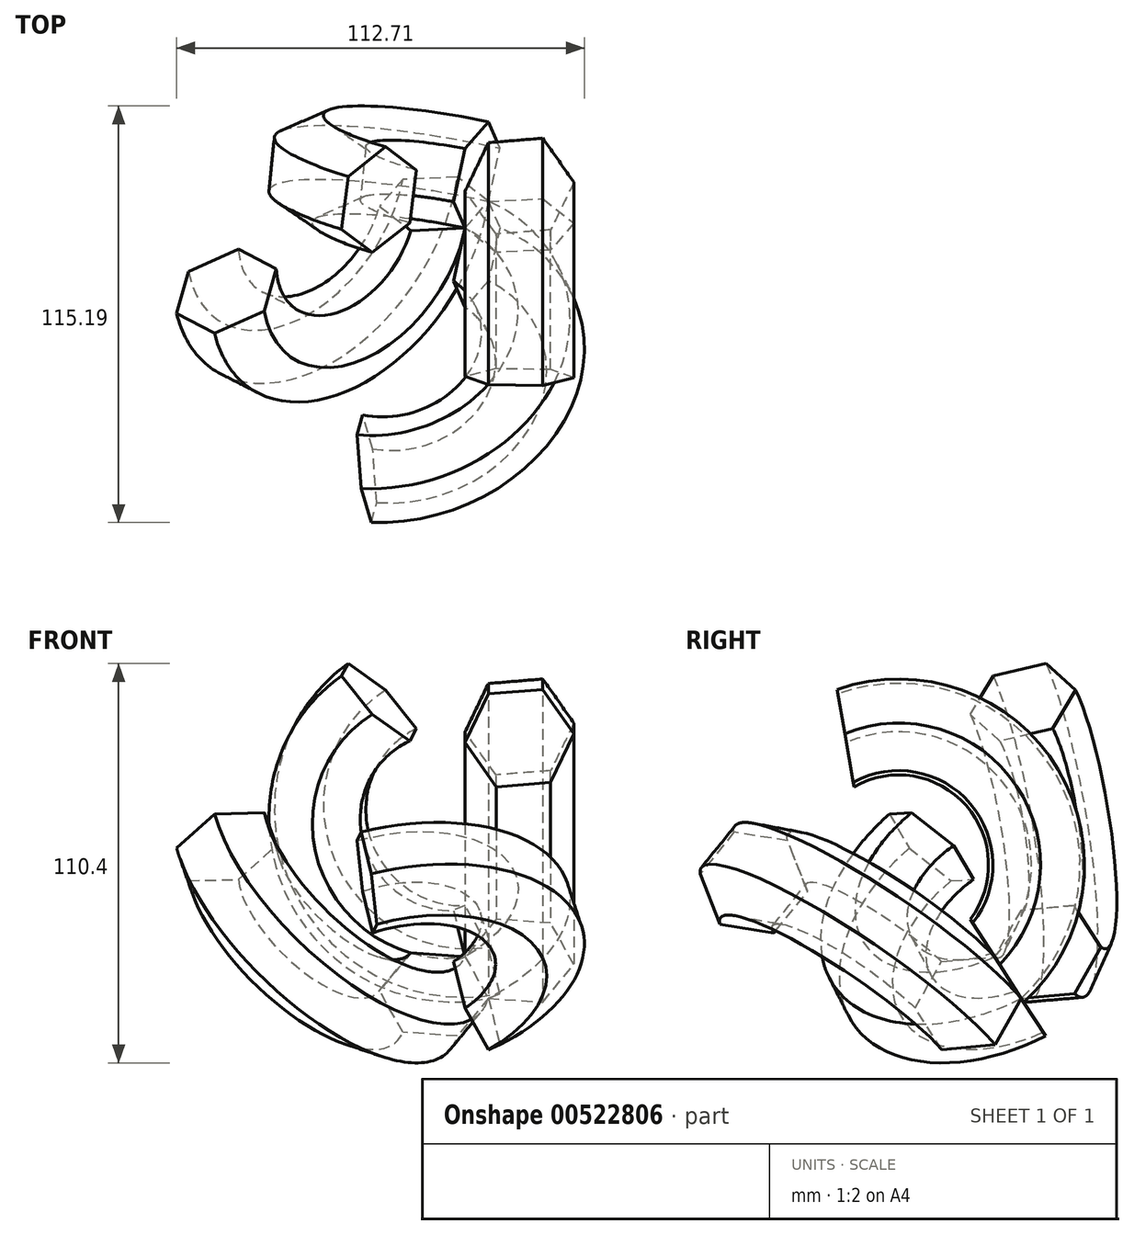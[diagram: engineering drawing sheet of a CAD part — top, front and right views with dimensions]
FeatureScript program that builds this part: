
annotation { "Feature Type Name" : "Feature", "Feature Type Description" : "" }
export const myFeature = defineFeature(function(context is Context, id is Id, definition is map)
    precondition{}
    {
        {
            var Q0;
            Q0=qCreatedBy(makeId("Top.planeOp"),FACE);
            var sketch = newSketch(context, id + "F0", { "sketchPlane" : qUnion([Q0])});
            skCircle(sketch, "E0.cCircle", {"center": v(-29.22, 20.18) * mm, "radius": 13.07 * mm, "construction": true});
            skLineSegment(sketch, "E0.0", {"start": v(-14.18, 21.44) * mm, "end": v(-20.6, 7.78) * mm});
            skLineSegment(sketch, "E0.1", {"start": v(-20.6, 7.78) * mm, "end": v(-35.65, 6.52) * mm});
            skLineSegment(sketch, "E0.2", {"start": v(-35.65, 6.52) * mm, "end": v(-44.26, 18.91) * mm});
            skLineSegment(sketch, "E0.3", {"start": v(-44.26, 18.91) * mm, "end": v(-37.84, 32.57) * mm});
            skLineSegment(sketch, "E0.4", {"start": v(-37.84, 32.57) * mm, "end": v(-22.8, 33.83) * mm});
            skLineSegment(sketch, "E0.5", {"start": v(-22.8, 33.83) * mm, "end": v(-14.18, 21.44) * mm});
            skPoint(sketch, "E0.0.midPoint", {"position": v(-17.4, 14.61) * mm});
            skSolve(sketch);
        }
        {
            var Q0;
            Q0=qCreatedBy(makeId("Right.planeOp"),FACE);
            var sketch = newSketch(context, id + "F1", { "sketchPlane" : qUnion([Q0])});
            skArc(sketch, "E1", {"start": v(-20.47, 12.8) * mm, "mid": v(-38.44, -7.8) * mm, "end": v(-21.86, -29.52) * mm});
            skSolve(sketch);
        }
        {
            var Q0;
            Q0=makeQuery(id+"F0.imprint","IMPRINT",FACE,{"disambiguationData":[TD([[makeQuery(id+"F0.imprint","IMPRINT",EDGE,{"derivedFrom":sQuery(id+"F0.wireOp",EDGE,"E0.0")}),-1.0]])]});
            var Q1;
            Q1=sQuery(id+"F1.wireOp",EDGE,"E1");
            sweep(context, id + "F2", {"profiles" : qUnion([Q0]), "path" : qUnion([Q1])});
        }
        {
            var Q0;
            Q0=makeQuery(id+"F2.opSweep","SWEPT_BODY",BODY,{"disambiguationData":[OSD([sQuery(id+"F0.wireOp",EDGE,"E0.0"),sQuery(id+"F0.wireOp",EDGE,"E0.1"),sQuery(id+"F0.wireOp",EDGE,"E0.2"),sQuery(id+"F0.wireOp",EDGE,"E0.3"),sQuery(id+"F0.wireOp",EDGE,"E0.4"),sQuery(id+"F0.wireOp",EDGE,"E0.5"),sQuery(id+"F1.wireOp",EDGE,"E1")])]});
            var Q1;
            Q1=makeQuery(id+"F2.opSweep","CAP_EDGE",EDGE,{"disambiguationData":[OSD([sQuery(id+"F0.wireOp",EDGE,"E0.3"),sQuery(id+"F1.wireOp",VERTEX,"E1.end")])],"isStart":false});
            circularPattern(context, id + "F3", {"entities" : qUnion([Q0]), "axis" : qUnion([Q1]), "angle" : 360 * degree, "instanceCount" : 4, "equalSpace" : true});
        }
    });
